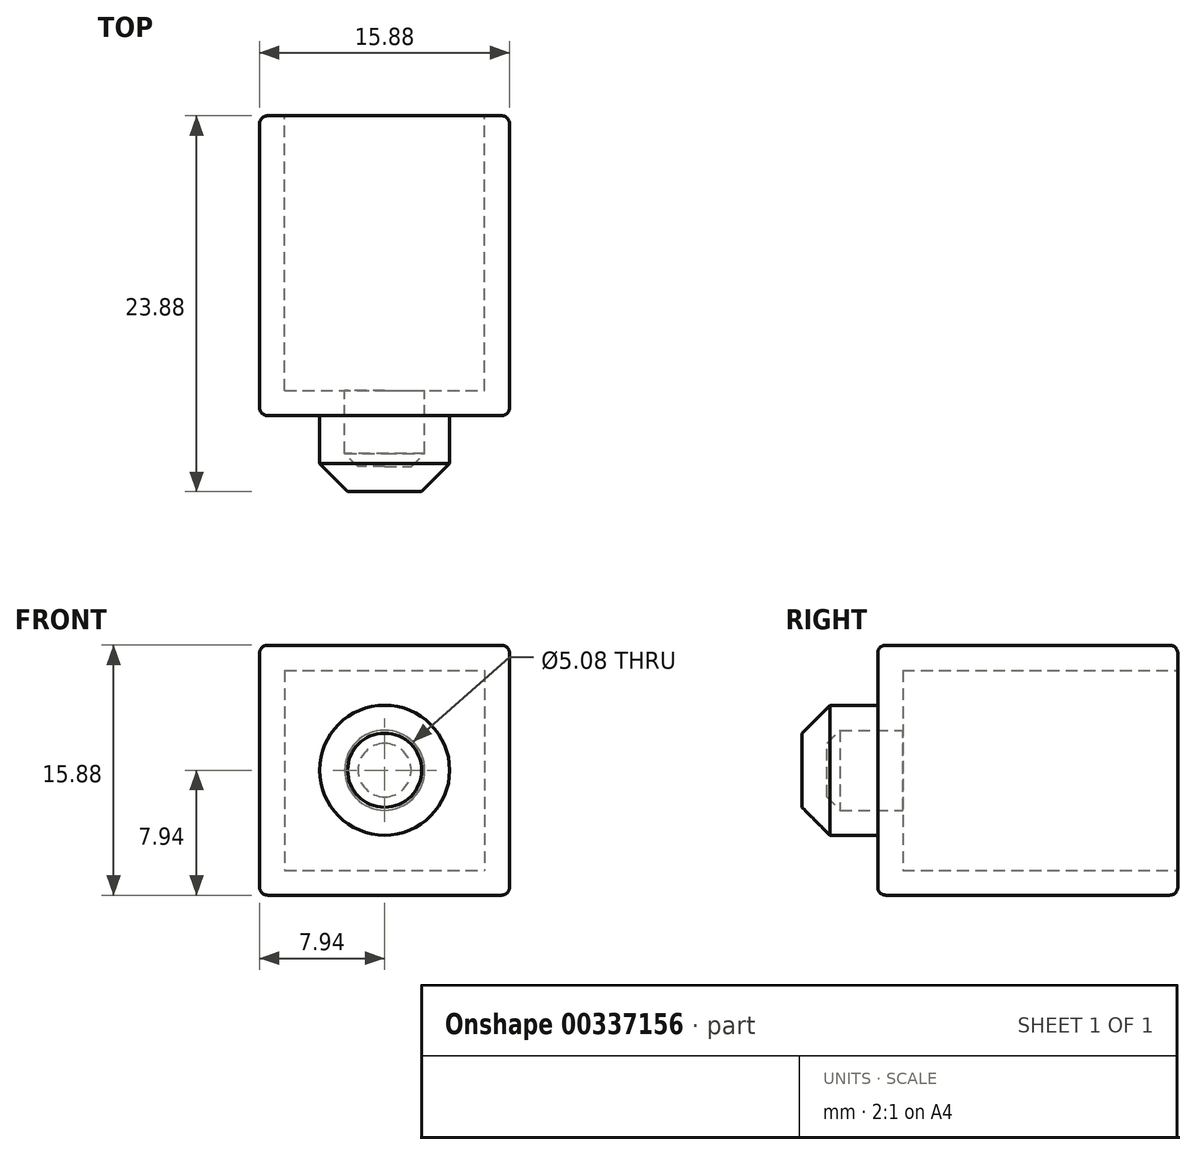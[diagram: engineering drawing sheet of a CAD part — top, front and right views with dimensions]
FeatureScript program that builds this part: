
annotation { "Feature Type Name" : "Feature", "Feature Type Description" : "" }
export const myFeature = defineFeature(function(context is Context, id is Id, definition is map)
    precondition{}
    {
        {
            var Q0;
            Q0=qCreatedBy(makeId("Front.planeOp"),FACE);
            var sketch = newSketch(context, id + "F0", { "sketchPlane" : qUnion([Q0])});
            skLineSegment(sketch, "E0.bottom", {"start": v(-7.94, 7.94) * mm, "end": v(7.94, 7.94) * mm});
            skLineSegment(sketch, "E0.top", {"start": v(-7.94, -7.94) * mm, "end": v(7.94, -7.94) * mm});
            skLineSegment(sketch, "E0.left", {"start": v(-7.94, 7.94) * mm, "end": v(-7.94, -7.94) * mm});
            skLineSegment(sketch, "E0.right", {"start": v(7.94, 7.94) * mm, "end": v(7.94, -7.94) * mm});
            skPoint(sketch, "E0.middle", {"position": v(0, 0) * mm});
            skSolve(sketch);
        }
        {
            var Q0;
            Q0 = qSketchRegion(id + "F0", true);
            extrude(context, id + "F1", {"entities" : qUnion([Q0]), "depth" : 19.05 * mm});
        }
        {
            var Q0;
            Q0=makeQuery(id+"F1.opExtrude","CAP_FACE",FACE,{"disambiguationData":[OSD([sQuery(id+"F0.wireOp",EDGE,"E0.bottom"),sQuery(id+"F0.wireOp",EDGE,"E0.top"),sQuery(id+"F0.wireOp",EDGE,"E0.left"),sQuery(id+"F0.wireOp",EDGE,"E0.right")])],"isStart":false});
            var sketch = newSketch(context, id + "F2", { "sketchPlane" : qUnion([Q0])});
            skCircle(sketch, "E1", {"center": v(0, 0) * mm, "radius": 4.13 * mm});
            skSolve(sketch);
        }
        {
            var Q0;
            Q0 = qSketchRegion(id + "F2", true);
            extrude(context, id + "F3", {"entities" : qUnion([Q0]), "operationType" : NewBodyOperationType.ADD, "depth" : 4.83 * mm});
        }
        {
            var Q0;
            Q0=makeQuery(id+"F3.opExtrude","CAP_FACE",FACE,{"disambiguationData":[OSD([sQuery(id+"F2.wireOp",EDGE,"E1")])],"isStart":false});
            chamfer(context, id + "F4", {"entities" : qUnion([Q0]), "width" : 1.78 * mm, "tangentPropagation" : true});
        }
        {
            var Q0;
            Q0=makeQuery(id+"F1.opExtrude","CAP_FACE",FACE,{"disambiguationData":[OSD([sQuery(id+"F0.wireOp",EDGE,"E0.bottom"),sQuery(id+"F0.wireOp",EDGE,"E0.top"),sQuery(id+"F0.wireOp",EDGE,"E0.left"),sQuery(id+"F0.wireOp",EDGE,"E0.right")])],"isStart":true});
            shell(context, id + "F5", {"entities" : qUnion([Q0]), "thickness" : 1.59 * mm});
        }
        {
            var Q0;
            Q0=makeQuery(id+"F1.opExtrude","CAP_EDGE",EDGE,{"disambiguationData":[OSD([sQuery(id+"F0.wireOp",EDGE,"E0.bottom")])],"isStart":false});
            var Q1;
            Q1=makeQuery(id+"F1.opExtrude","CAP_EDGE",EDGE,{"disambiguationData":[OSD([sQuery(id+"F0.wireOp",EDGE,"E0.left")])],"isStart":false});
            var Q2;
            Q2=makeQuery(id+"F1.opExtrude","CAP_EDGE",EDGE,{"disambiguationData":[OSD([sQuery(id+"F0.wireOp",EDGE,"E0.top")])],"isStart":false});
            var Q3;
            Q3=makeQuery(id+"F1.opExtrude","CAP_EDGE",EDGE,{"disambiguationData":[OSD([sQuery(id+"F0.wireOp",EDGE,"E0.right")])],"isStart":false});
            var Q4;
            Q4=makeQuery(id+"F1.opExtrude","SWEPT_EDGE",EDGE,{"disambiguationData":[OSD([sQuery(id+"F0.wireOp",EDGE,"E0.bottom"),sQuery(id+"F0.wireOp",EDGE,"E0.left")])]});
            var Q5;
            Q5=makeQuery(id+"F1.opExtrude","SWEPT_EDGE",EDGE,{"disambiguationData":[OSD([sQuery(id+"F0.wireOp",EDGE,"E0.top"),sQuery(id+"F0.wireOp",EDGE,"E0.left")])]});
            var Q6;
            Q6=makeQuery(id+"F1.opExtrude","SWEPT_EDGE",EDGE,{"disambiguationData":[OSD([sQuery(id+"F0.wireOp",EDGE,"E0.bottom"),sQuery(id+"F0.wireOp",EDGE,"E0.right")])]});
            var Q7;
            Q7=makeQuery(id+"F1.opExtrude","SWEPT_EDGE",EDGE,{"disambiguationData":[OSD([sQuery(id+"F0.wireOp",EDGE,"E0.top"),sQuery(id+"F0.wireOp",EDGE,"E0.right")])]});
            var Q8;
            Q8=makeQuery(id+"F1.opExtrude","CAP_EDGE",EDGE,{"disambiguationData":[OSD([sQuery(id+"F0.wireOp",EDGE,"E0.top")])],"isStart":true});
            var Q9;
            Q9=makeQuery(id+"F1.opExtrude","CAP_EDGE",EDGE,{"disambiguationData":[OSD([sQuery(id+"F0.wireOp",EDGE,"E0.right")])],"isStart":true});
            var Q10;
            Q10=makeQuery(id+"F1.opExtrude","CAP_EDGE",EDGE,{"disambiguationData":[OSD([sQuery(id+"F0.wireOp",EDGE,"E0.bottom")])],"isStart":true});
            var Q11;
            Q11=makeQuery(id+"F1.opExtrude","CAP_EDGE",EDGE,{"disambiguationData":[OSD([sQuery(id+"F0.wireOp",EDGE,"E0.left")])],"isStart":true});
            fillet(context, id + "F6", {"entities" : qUnion([Q0, Q1, Q2, Q3, Q4, Q5, Q6, Q7, Q8, Q9, Q10, Q11]), "radius" : 0.5 * mm, "tangentPropagation" : true, "allowEdgeOverflow" : false});
        }
    });
